# Revit family: Dishwasher_Cmrcl-Line
name_source: partatom
category: Specialty Equipment
revit_build: Autodesk Revit Architecture 2012 (Build: 20110309_2315)
units: mm (PartAtom-declared; Revit-internal decimal feet)

## types (2) — shared parameters
Assembly Code = E1090320
Body Material = ARCAT - Metal - Stainless Steel - 304 - Satin
Cleaning Method = Low Temperature Chemical Sanitizing
Conformance = ASTM F 1920
Construction Details = http://www.arcat.com
Depth = 2' - 0"
Description = Commercial Line Dishwasher
Estar = Compliant
Expected Lifespan (Years) = 10
Frame Material = ARCAT - Metal - Stainless Steel - 304 - Satin
Green Building-LEED = http://www.arcat.com
Guards = ARCAT - Plastic - ABS - Black
Height = 3' - 0"
Keynote = 11440
Lenght = 8' - 0"
Maintenance Schedule (Months) = 2
Manufacturer = Generic
Manufacturer Fax = (203) 939-2444
Manufacturer Website = http://www.arcat.com
Max Conveyor Speed_Ft_Min = 4
Model = Generic
Product Data = http://www.arcat.com
Product Properties = http://www.arcat.com
Refuse Collector = ARCAT - Plastic - HDPE - Brown
Specification = http://www.arcat.com
Usage_Gal per Rack = 0.5
Warranty Duration (Years) = 2
Water Usage_GPH = 15
Work Surfaces = ARCAT - Metal - Stainless Steel - 304 - Satin
zero-valued in all types: clnmth

## type names (no varying parameters)
- HIgh Temp Sanitizer
- Chemical Sanitizer

## geometry (parser evidence)
native form markers: Sweep x1
no freeform markers — native parametric forms only
